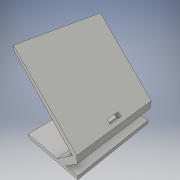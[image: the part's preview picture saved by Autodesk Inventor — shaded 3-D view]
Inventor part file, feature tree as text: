
AUTODESK INVENTOR PART (.ipt)
format: ipt  version: 2016 (Build 200138000, 138)  size: 122,368 bytes
history: native  units: in
note: dims shown in document units (in); Inventor stores cm internally (conversion verified against a paired STEP export)
features: extrude x2, sketch x2
ambient origin geometry x8: Origin, YZ Plane, XZ Plane, XY Plane, X Axis, Y Axis, Z Axis, Center Point
bodies: Solid1 (feature_tree)
feature tree (4):
  extrude  "Extrusion1"  TaperAngle=45.0deg  [1 undecoded]
  extrude  "Extrusion4"  Depth=0.75in
  sketch  "Sketch1"  dims[d0=5.0in d1=45.0deg]
  sketch  "Sketch4"  dims[d2=0.25in d4=0.75in d5=0.5in d6=90.0deg d7=0.25in d8=90.0deg d9=135.0deg d10=0.4in d11=135.0deg d12=5.0in d13=0.0in d22=0.2in d23=90.0deg d24=0.75in d25=0.25in d26=1.0in d27=0.0in]
note: 1 required parameter value undecoded (feature->parameter linkage not recoverable at this tier; creation-order binding heuristic only, values carry confidence <= 0.55)
